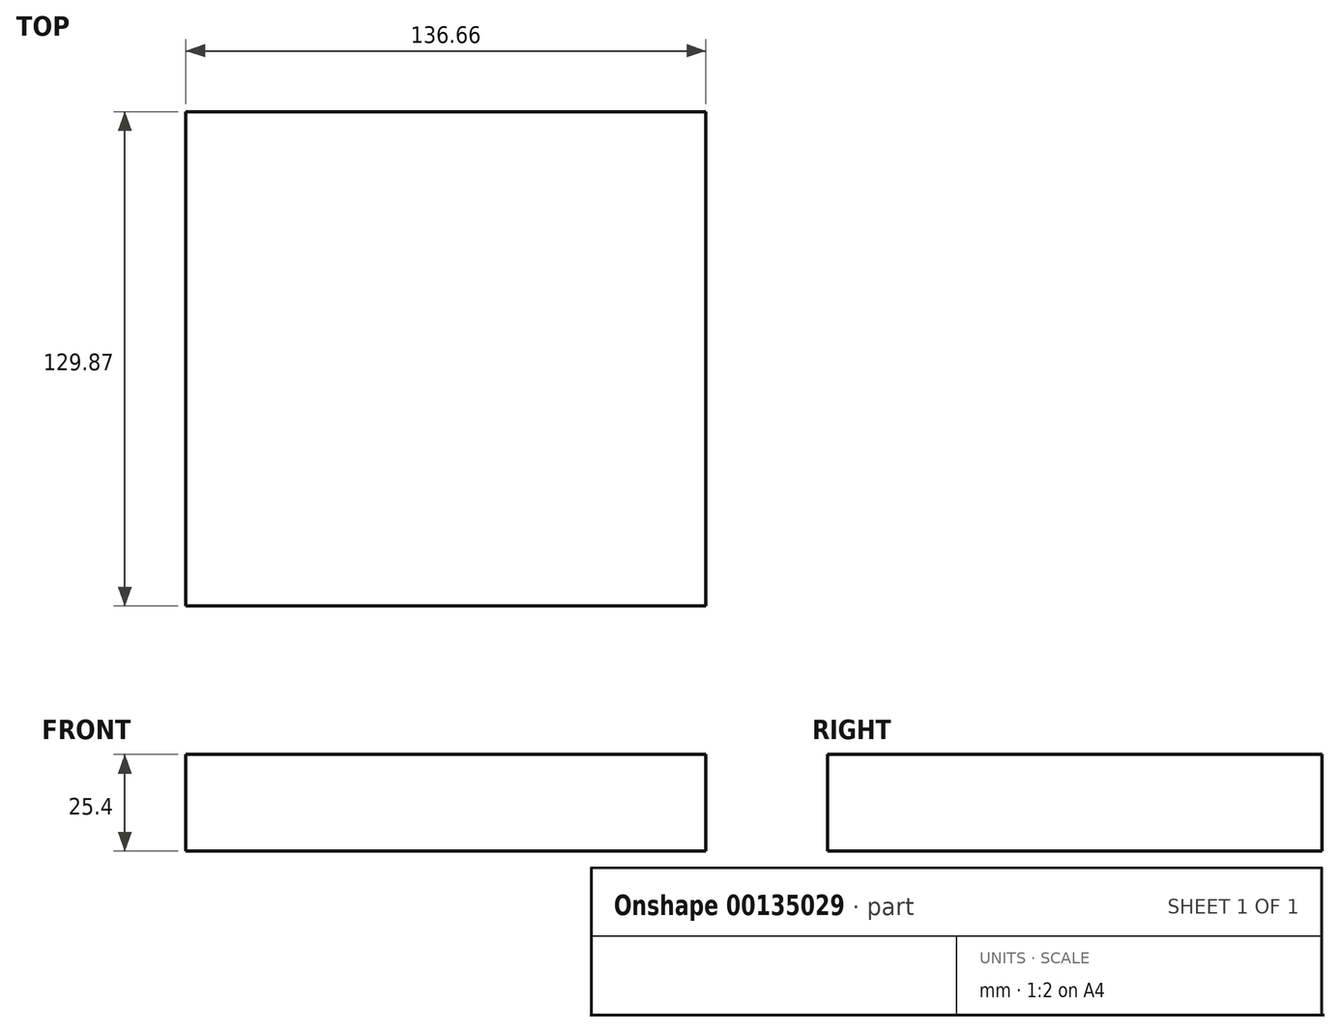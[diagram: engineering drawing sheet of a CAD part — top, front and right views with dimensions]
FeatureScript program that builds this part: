
annotation { "Feature Type Name" : "Feature", "Feature Type Description" : "" }
export const myFeature = defineFeature(function(context is Context, id is Id, definition is map)
    precondition{}
    {
        {
            var Q0;
            Q0=qCreatedBy(makeId("Top.planeOp"),FACE);
            var sketch = newSketch(context, id + "F0", { "sketchPlane" : qUnion([Q0])});
            skLineSegment(sketch, "E0.bottom", {"start": v(-87.1, -109.65) * mm, "end": v(49.55, -109.65) * mm});
            skLineSegment(sketch, "E0.top", {"start": v(-87.1, 20.22) * mm, "end": v(49.55, 20.22) * mm});
            skLineSegment(sketch, "E0.left", {"start": v(-87.1, -109.65) * mm, "end": v(-87.1, 20.22) * mm});
            skLineSegment(sketch, "E0.right", {"start": v(49.55, -109.65) * mm, "end": v(49.55, 20.22) * mm});
            skSolve(sketch);
        }
        {
            var Q0;
            Q0 = qSketchRegion(id + "F0", true);
            extrude(context, id + "F1", {"entities" : qUnion([Q0]), "depth" : 25.4 * mm});
        }
    });
